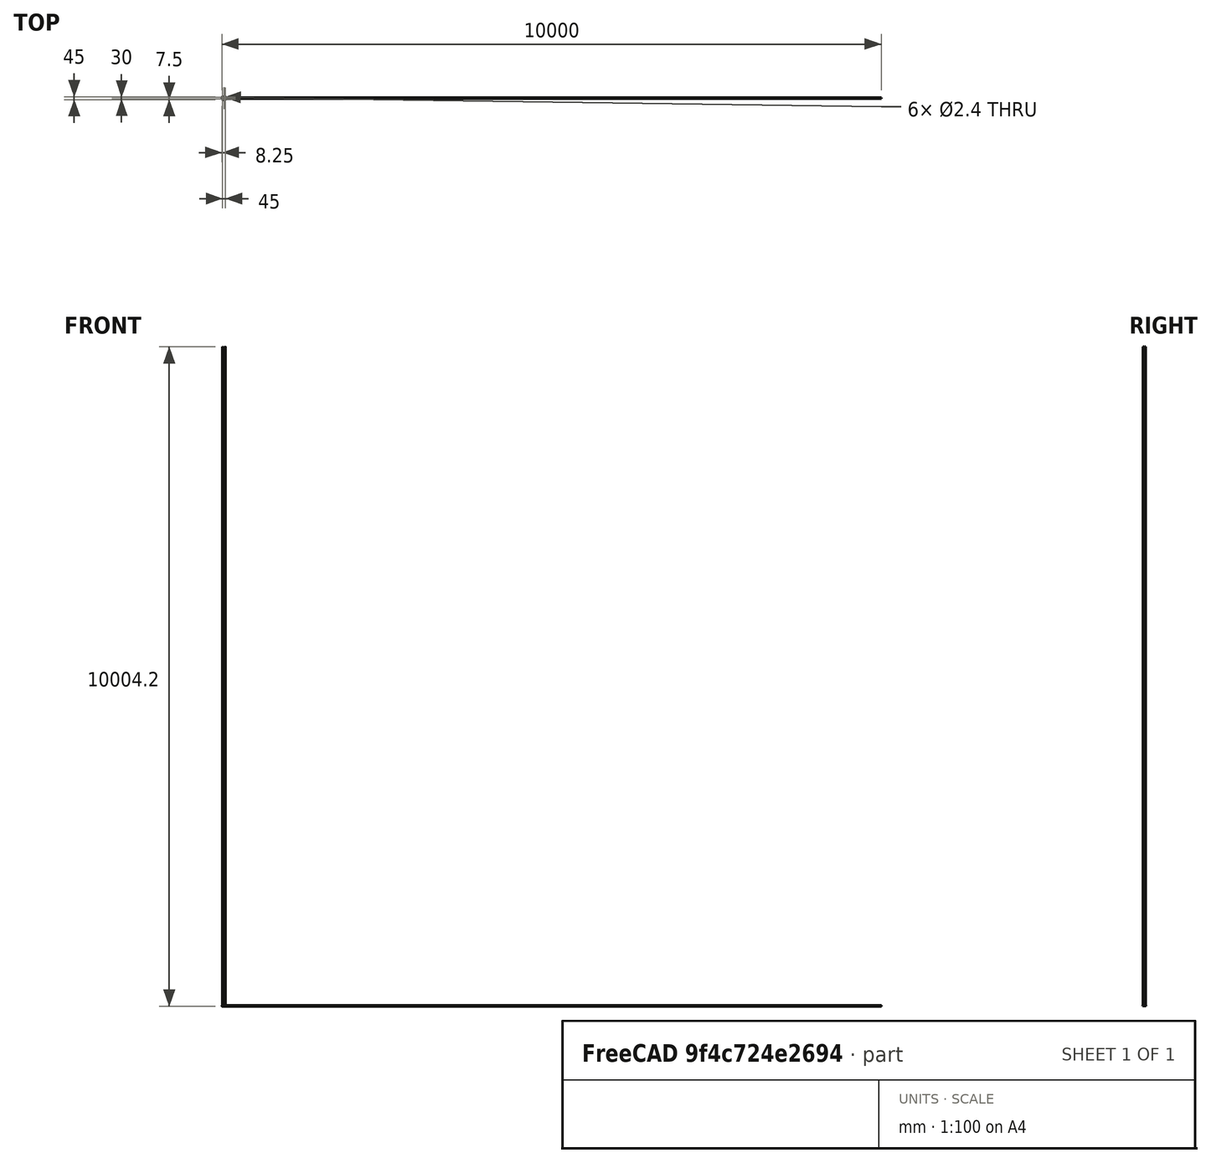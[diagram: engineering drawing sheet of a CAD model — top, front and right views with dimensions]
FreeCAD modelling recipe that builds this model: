
FCSTD DOCUMENT  (FreeCAD 0.16R)
Label: 60mmPed3
License: All rights reserved
LicenseURL: http://en.wikipedia.org/wiki/All_rights_reserved
objects: Sketcher::SketchObject×4, PartDesign::Pocket×3, PartDesign::Chamfer×2, PartDesign::Pad×1, Mesh::Feature×1
note: 14 computed .brp shape members not serialized (recipe doc carries the construction recipe); baked Part::Feature solids carry a one-line shape summary decoded from their .brp

FEATURE [Sketcher::SketchObject] Sketch
  sketch-geometry (8):
    g0: LineSegment StartX=25.75 StartY=-12.5 StartZ=0 EndX=25.75 EndY=12.5 EndZ=0
    g1: LineSegment StartX=15.75 StartY=22.5 StartZ=0 EndX=-15.75 EndY=22.5 EndZ=0
    g2: LineSegment StartX=15.75 StartY=-22.5 StartZ=0 EndX=-15.75 EndY=-22.5 EndZ=0
    g3: LineSegment StartX=-33.25 StartY=5 StartZ=0 EndX=-33.25 EndY=-5 EndZ=0
    g4: ArcOfCircle CenterX=-15.75 CenterY=5 CenterZ=0 NormalX=0 NormalY=0 NormalZ=1 Radius=17.5 StartAngle=1.5708 EndAngle=3.14159
    g5: ArcOfCircle CenterX=-15.75 CenterY=-5 CenterZ=0 NormalX=0 NormalY=0 NormalZ=1 Radius=17.5 StartAngle=3.14159 EndAngle=4.71239
    g6: ArcOfCircle CenterX=15.75 CenterY=-12.5 CenterZ=0 NormalX=0 NormalY=0 NormalZ=1 Radius=10 StartAngle=4.71239 EndAngle=6.28319
    g7: ArcOfCircle CenterX=15.75 CenterY=12.5 CenterZ=0 NormalX=0 NormalY=0 NormalZ=1 Radius=10 StartAngle=0 EndAngle=1.5708
  constraints (20):
    c: Horizontal(g1)
    c: Horizontal(g2)
    c: Equal(g2,g1)
    c: Tangent(g3,g4) = -1.5708
    c: Tangent(g1,g4) = -1.5708
    c: Tangent(g3,g5) = -1.5708
    c: Tangent(g2,g5) = 1.5708
    c: Tangent(g2,g6) = 1.5708
    c: Tangent(g0,g6) = -1.5708
    c: Tangent(g1,g7) = -1.5708
    c: Tangent(g0,g7) = -1.5708
    c: Vertical(g3)
    c: Vertical(g0)
    c: Symmetric(g3,g3,g-1)
    c: Symmetric(g0,g0,g-1)
    c: Symmetric(g1,g1,g-2)
    c: Distance(g0,g3) = 59
    c: Distance(g1,g2) = 45
    c: Distance(g3) = 10
    c: Distance(g0) = 25
FEATURE [PartDesign::Pad] Pad
  Length = 6
  Length2 = 100
  Sketch = -> Sketch
  Type = 0
FEATURE [Sketcher::SketchObject] Sketch002
  Placement = pos=(-33.25,0,0) rot=(0.57735,-0.57735,-0.57735;2.0944rad)
  Support = -> Pad [Face6]
  sketch-geometry (1):
    g0: Circle CenterX=0 CenterY=0 CenterZ=0 NormalX=0 NormalY=0 NormalZ=1 Radius=4.2
  constraints (2):
    c: Radius(g0) = 4.2
    c: Coincident(g0,g-1)
FEATURE [PartDesign::Pocket] Pocket
  Length = 5
  Sketch = -> Sketch002
  Type = 1
FEATURE [Sketcher::SketchObject] Sketch006
  Placement = pos=(0,0,0) rot=(1,0,0;3.14159rad)
  Support = -> Pocket [Face4]
  sketch-geometry (6):
    g0: Circle CenterX=-25 CenterY=10 CenterZ=0 NormalX=0 NormalY=0 NormalZ=1 Radius=1.2
    g1: Circle CenterX=0 CenterY=-15 CenterZ=0 NormalX=0 NormalY=0 NormalZ=1 Radius=1.2
    g2: Circle CenterX=0 CenterY=15 CenterZ=0 NormalX=0 NormalY=0 NormalZ=1 Radius=1.2
    g3: Circle CenterX=-25 CenterY=-10 CenterZ=0 NormalX=0 NormalY=0 NormalZ=1 Radius=1.2
    g4: Circle CenterX=20 CenterY=10 CenterZ=0 NormalX=0 NormalY=0 NormalZ=1 Radius=1.2
    g5: Circle CenterX=20 CenterY=-10 CenterZ=0 NormalX=0 NormalY=0 NormalZ=1 Radius=1.2
  constraints (16):
    c: Radius(g1) = 1.2
    c: Equal(g1,g0)
    c: Equal(g1,g2)
    c: Equal(g1,g3)
    c: Equal(g1,g5)
    c: Equal(g1,g4)
    c: PointOnObject(g1,g-2)
    c: PointOnObject(g2,g-2)
    c: Symmetric(g5,g4,g-1)
    c: Symmetric(g3,g0,g-1)
    c: Distance(g0,g3) = 20
    c: Distance(g4,g5) = 20
    c: DistanceX(g4) = 20
    c: DistanceX(g0) = -25
    c: Symmetric(g1,g2,g-1)
    c: Distance(g1,g2) = 30
FEATURE [PartDesign::Pocket] Pocket001
  Length = 5
  Sketch = -> Sketch006
  Type = 1
FEATURE [Sketcher::SketchObject] Sketch007
  Placement = pos=(0,0,6) rot=(0,0,1;0rad)
  Support = -> Pocket001 [Face5]
  sketch-geometry (42):
    g0: LineSegment StartX=-25 StartY=7.57513 StartZ=0 EndX=-22.9 EndY=8.78756 EndZ=0
    g1: LineSegment StartX=-22.9 StartY=8.78756 StartZ=0 EndX=-22.9 EndY=11.2124 EndZ=0
    g2: LineSegment StartX=-22.9 StartY=11.2124 StartZ=0 EndX=-25 EndY=12.4249 EndZ=0
    g3: LineSegment StartX=-25 StartY=12.4249 StartZ=0 EndX=-27.1 EndY=11.2124 EndZ=0
    g4: LineSegment StartX=-27.1 StartY=11.2124 StartZ=0 EndX=-27.1 EndY=8.78756 EndZ=0
    g5: LineSegment StartX=-27.1 StartY=8.78756 StartZ=0 EndX=-25 EndY=7.57513 EndZ=0
    g6: Circle [constr] CenterX=-25 CenterY=10 CenterZ=0 NormalX=0 NormalY=0 NormalZ=1 Radius=2.42487
    g7: LineSegment StartX=-3.46023e-07 StartY=-17.4249 StartZ=0 EndX=2.1 EndY=-16.2124 EndZ=0
    g8: LineSegment StartX=2.1 StartY=-16.2124 StartZ=0 EndX=2.1 EndY=-13.7876 EndZ=0
    g9: LineSegment StartX=2.1 StartY=-13.7876 StartZ=0 EndX=-3.46023e-07 EndY=-12.5751 EndZ=0
    g10: LineSegment StartX=-3.46023e-07 StartY=-12.5751 StartZ=0 EndX=-2.1 EndY=-13.7876 EndZ=0
    g11: LineSegment StartX=-2.1 StartY=-13.7876 StartZ=0 EndX=-2.1 EndY=-16.2124 EndZ=0
    g12: LineSegment StartX=-2.1 StartY=-16.2124 StartZ=0 EndX=-3.46023e-07 EndY=-17.4249 EndZ=0
    g13: Circle [constr] CenterX=-3.46023e-07 CenterY=-15 CenterZ=0 NormalX=0 NormalY=0 NormalZ=1 Radius=2.42487
    g14: LineSegment StartX=-25 StartY=-12.4249 StartZ=0 EndX=-22.9 EndY=-11.2124 EndZ=0
    g15: LineSegment StartX=-22.9 StartY=-11.2124 StartZ=0 EndX=-22.9 EndY=-8.78756 EndZ=0
    g16: LineSegment StartX=-22.9 StartY=-8.78756 StartZ=0 EndX=-25 EndY=-7.57513 EndZ=0
    g17: LineSegment StartX=-25 StartY=-7.57513 StartZ=0 EndX=-27.1 EndY=-8.78756 EndZ=0
    g18: LineSegment StartX=-27.1 StartY=-8.78756 StartZ=0 EndX=-27.1 EndY=-11.2124 EndZ=0
    g19: LineSegment StartX=-27.1 StartY=-11.2124 StartZ=0 EndX=-25 EndY=-12.4249 EndZ=0
    g20: Circle [constr] CenterX=-25 CenterY=-10 CenterZ=0 NormalX=0 NormalY=0 NormalZ=1 Radius=2.42487
    g21: LineSegment StartX=1.38641e-06 StartY=12.5751 StartZ=0 EndX=2.1 EndY=13.7876 EndZ=0
    g22: LineSegment StartX=2.1 StartY=13.7876 StartZ=0 EndX=2.1 EndY=16.2124 EndZ=0
    g23: LineSegment StartX=2.1 StartY=16.2124 StartZ=0 EndX=1.38641e-06 EndY=17.4249 EndZ=0
    g24: LineSegment StartX=1.38641e-06 StartY=17.4249 StartZ=0 EndX=-2.1 EndY=16.2124 EndZ=0
    g25: LineSegment StartX=-2.1 StartY=16.2124 StartZ=0 EndX=-2.1 EndY=13.7876 EndZ=0
    g26: LineSegment StartX=-2.1 StartY=13.7876 StartZ=0 EndX=1.38641e-06 EndY=12.5751 EndZ=0
    g27: Circle [constr] CenterX=1.38641e-06 CenterY=15 CenterZ=0 NormalX=0 NormalY=0 NormalZ=1 Radius=2.42487
    g28: LineSegment StartX=20 StartY=-12.4249 StartZ=0 EndX=22.1 EndY=-11.2124 EndZ=0
    g29: LineSegment StartX=22.1 StartY=-11.2124 StartZ=0 EndX=22.1 EndY=-8.78756 EndZ=0
    g30: LineSegment StartX=22.1 StartY=-8.78756 StartZ=0 EndX=20 EndY=-7.57513 EndZ=0
    g31: LineSegment StartX=20 StartY=-7.57513 StartZ=0 EndX=17.9 EndY=-8.78756 EndZ=0
    g32: LineSegment StartX=17.9 StartY=-8.78756 StartZ=0 EndX=17.9 EndY=-11.2124 EndZ=0
    g33: LineSegment StartX=17.9 StartY=-11.2124 StartZ=0 EndX=20 EndY=-12.4249 EndZ=0
    g34: Circle [constr] CenterX=20 CenterY=-10 CenterZ=0 NormalX=0 NormalY=0 NormalZ=1 Radius=2.42487
    g35: LineSegment StartX=20 StartY=7.57513 StartZ=0 EndX=22.1 EndY=8.78757 EndZ=0
    g36: LineSegment StartX=22.1 StartY=8.78757 StartZ=0 EndX=22.1 EndY=11.2124 EndZ=0
    g37: LineSegment StartX=22.1 StartY=11.2124 StartZ=0 EndX=20 EndY=12.4249 EndZ=0
    g38: LineSegment StartX=20 StartY=12.4249 StartZ=0 EndX=17.9 EndY=11.2124 EndZ=0
    g39: LineSegment StartX=17.9 StartY=11.2124 StartZ=0 EndX=17.9 EndY=8.78757 EndZ=0
    g40: LineSegment StartX=17.9 StartY=8.78757 StartZ=0 EndX=20 EndY=7.57513 EndZ=0
    g41: Circle [constr] CenterX=20 CenterY=10 CenterZ=0 NormalX=0 NormalY=0 NormalZ=1 Radius=2.42487
  constraints (90):
    c: Coincident(g0,g1)
    c: Coincident(g1,g2)
    c: Coincident(g2,g3)
    c: Coincident(g3,g4)
    c: Coincident(g4,g5)
    c: Coincident(g5,g0)
    c: Equal(g0, g1-g5) x5
    c: PointOnObject(g0,g6)
    c: PointOnObject(g1,g6)
    c: PointOnObject(g2,g6)
    c: PointOnObject(g3,g6)
    c: PointOnObject(g4,g6)
    c: PointOnObject(g5,g6)
    c: Distance(g0,g3) = 4.2
    c: Coincident(g7,g8)
    c: Coincident(g8,g9)
    c: Coincident(g9,g10)
    c: Coincident(g10,g11)
    c: Coincident(g11,g12)
    c: Coincident(g12,g7)
    c: Equal(g7, g8-g12) x5
    c: PointOnObject(g7,g13)
    c: PointOnObject(g8,g13)
    c: PointOnObject(g9,g13)
    c: PointOnObject(g10,g13)
    c: PointOnObject(g11,g13)
    c: PointOnObject(g12,g13)
    c: Coincident(g14,g15)
    c: Coincident(g15,g16)
    c: Coincident(g16,g17)
    c: Coincident(g17,g18)
    c: Coincident(g18,g19)
    c: Coincident(g19,g14)
    c: Equal(g14, g15-g19) x5
    c: PointOnObject(g14,g20)
    c: PointOnObject(g15,g20)
    c: PointOnObject(g16,g20)
    c: PointOnObject(g17,g20)
    c: PointOnObject(g18,g20)
    c: PointOnObject(g19,g20)
    c: Coincident(g21,g22)
    c: Coincident(g22,g23)
    c: Coincident(g23,g24)
    c: Coincident(g24,g25)
    c: Coincident(g25,g26)
    c: Coincident(g26,g21)
    c: Equal(g21, g22-g26) x5
    c: PointOnObject(g21,g27)
    c: PointOnObject(g22,g27)
    c: PointOnObject(g23,g27)
    c: PointOnObject(g24,g27)
    c: PointOnObject(g25,g27)
    c: PointOnObject(g26,g27)
    c: Distance(g21,g24) = 4.2
    c: Distance(g14,g17) = 4.2
    c: Distance(g7,g10) = 4.2
    c: Coincident(g28,g29)
    c: Coincident(g29,g30)
    c: Coincident(g30,g31)
    c: Coincident(g31,g32)
    c: Coincident(g32,g33)
    c: Coincident(g33,g28)
    c: Equal(g28, g29-g33) x5
    c: PointOnObject(g28,g34)
    c: PointOnObject(g29,g34)
    c: PointOnObject(g30,g34)
    c: PointOnObject(g31,g34)
    c: PointOnObject(g32,g34)
    c: PointOnObject(g33,g34)
    c: Coincident(g35,g36)
    c: Coincident(g36,g37)
    c: Coincident(g37,g38)
    c: Coincident(g38,g39)
    c: Coincident(g39,g40)
    c: Coincident(g40,g35)
    c: Equal(g35, g36-g40) x5
    c: PointOnObject(g35,g41)
    c: PointOnObject(g36,g41)
    c: PointOnObject(g37,g41)
    c: PointOnObject(g38,g41)
    c: PointOnObject(g39,g41)
    c: PointOnObject(g40,g41)
    c: Distance(g35,g37) = 4.2
    c: Distance(g28,g30) = 4.2
    c: Vertical(g1)
    c: Vertical(g22)
    c: Vertical(g8)
    c: Vertical(g29)
    c: Vertical(g36)
    c: Vertical(g15)
FEATURE [PartDesign::Pocket] Pocket002
  Length = 2
  Sketch = -> Sketch007
  Type = 0
FEATURE [PartDesign::Chamfer] Chamfer
  Base = -> Pocket002 [Edge152,Edge154,Edge156,Edge77,Edge75,Edge73]
  Size = 0.8
FEATURE [PartDesign::Chamfer] Chamfer001
  Base = -> Chamfer [Edge53]
  Size = 0.6
FEATURE [Mesh::Feature] Mesh  label="Chamfer001 (Meshed)"
